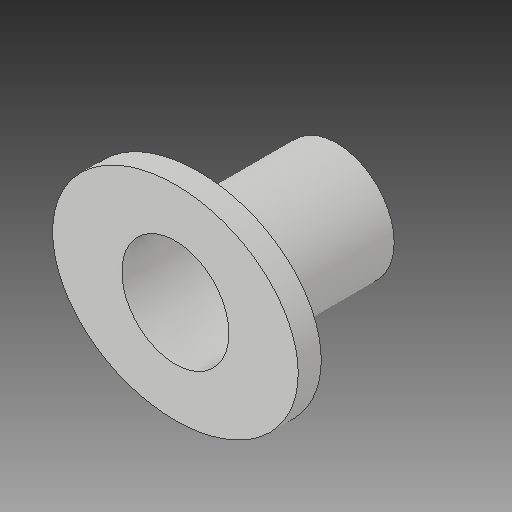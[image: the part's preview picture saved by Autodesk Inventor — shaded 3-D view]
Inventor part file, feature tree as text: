
AUTODESK INVENTOR PART (.ipt)
format: ipt  version: 2018 (Build 220112000, 112)  size: 118,272 bytes
history: native  units: mm
features: extrude x4, sketch x4, other x2, reference x1, projected_geometry x1
ambient origin geometry x8: Origin, YZ Plane, XZ Plane, XY Plane, X Axis, Y Axis, Z Axis, Center Point
bodies: Solid1 (feature_tree)
feature tree (12):
  extrude  "Extrusion1"  Depth=1.0mm TaperAngle=0.0deg
  extrude  "Extrusion2"  Depth=1.0mm TaperAngle=0.0deg
  extrude  "Extrusion3"  [1 undecoded]
  extrude  "Extrusion4"  [1 undecoded]
  sketch  "Sketch1"  dims[d0=5.0mm d1=0.0mm d2=1.0mm d3=0.0mm]
  reference  "Reference1"
  sketch  "Sketch2"  dims[d4=1.0mm d5=0.0mm d6=1.0mm d7=0.0mm]
  projected_geometry  "Projected Loop1"
  sketch  "Sketch3"
  sketch  "Sketch4"
  other  "Assembly1"
  other  "Pushfit-Adapter:1"
note: 2 required parameter values undecoded (feature->parameter linkage not recoverable at this tier; creation-order binding heuristic only, values carry confidence <= 0.55)
